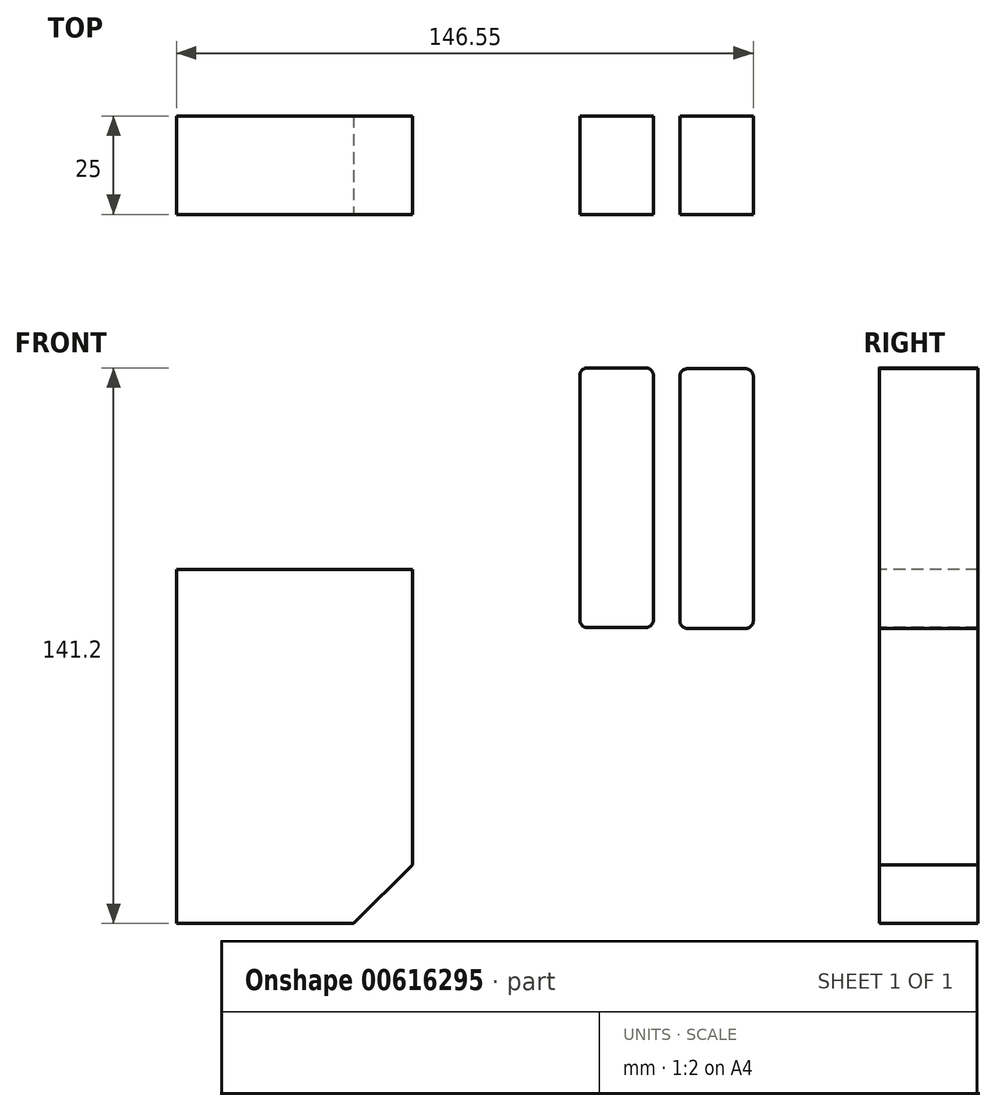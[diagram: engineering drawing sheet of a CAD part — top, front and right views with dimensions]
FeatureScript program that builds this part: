
annotation { "Feature Type Name" : "Feature", "Feature Type Description" : "" }
export const myFeature = defineFeature(function(context is Context, id is Id, definition is map)
    precondition{}
    {
        {
            var Q0;
            Q0=qCreatedBy(makeId("Front.planeOp"),FACE);
            var sketch = newSketch(context, id + "F0", { "sketchPlane" : qUnion([Q0])});
            skLineSegment(sketch, "E0.0", {"start": v(0, -90) * mm, "end": v(45, -90) * mm});
            skLineSegment(sketch, "E0.1", {"start": v(0, 0) * mm, "end": v(0, -90) * mm});
            skLineSegment(sketch, "E0.2", {"start": v(45, -90) * mm, "end": v(60, -75.15) * mm});
            skLineSegment(sketch, "E0.3", {"start": v(60, -75.15) * mm, "end": v(60, 0) * mm});
            skLineSegment(sketch, "E0.4", {"start": v(60, 0) * mm, "end": v(0, 0) * mm});
            skLineSegment(sketch, "E1.bottom", {"start": v(102.46, 51.2) * mm, "end": v(121.16, 51.2) * mm});
            skLineSegment(sketch, "E1.top", {"start": v(102.46, -14.8) * mm, "end": v(121.16, -14.8) * mm});
            skLineSegment(sketch, "E1.left", {"start": v(102.46, 51.2) * mm, "end": v(102.46, -14.8) * mm});
            skLineSegment(sketch, "E1.right", {"start": v(121.16, 51.2) * mm, "end": v(121.16, -14.8) * mm});
            skLineSegment(sketch, "E2.bottom", {"start": v(127.85, 50.99) * mm, "end": v(146.55, 50.99) * mm});
            skLineSegment(sketch, "E2.top", {"start": v(127.85, -15.01) * mm, "end": v(146.55, -15.01) * mm});
            skLineSegment(sketch, "E2.left", {"start": v(127.85, 50.99) * mm, "end": v(127.85, -15.01) * mm});
            skLineSegment(sketch, "E2.right", {"start": v(146.55, 50.99) * mm, "end": v(146.55, -15.01) * mm});
            skLineSegment(sketch, "E3.0", {"start": v(43.77, -87) * mm, "end": v(57, -73.9) * mm});
            skLineSegment(sketch, "E3.1", {"start": v(3, -87) * mm, "end": v(43.77, -87) * mm});
            skLineSegment(sketch, "E3.2", {"start": v(57, -73.9) * mm, "end": v(57, -3) * mm});
            skLineSegment(sketch, "E3.3", {"start": v(57, -3) * mm, "end": v(3, -3) * mm});
            skLineSegment(sketch, "E3.4", {"start": v(3, -3) * mm, "end": v(3, -87) * mm});
            skSolve(sketch);
        }
        {
            var Q0;
            Q0=sQuery(id+"F0.wireOp",EDGE,"E2.right");
            var Q1;
            Q1=sQuery(id+"F0.wireOp",EDGE,"E1.top");
            var Q2;
            Q2=sQuery(id+"F0.wireOp",EDGE,"E1.bottom");
            var Q3;
            Q3=sQuery(id+"F0.wireOp",EDGE,"E2.top");
            var Q4;
            Q4=sQuery(id+"F0.wireOp",EDGE,"E2.left");
            var Q5;
            Q5=sQuery(id+"F0.wireOp",EDGE,"E1.right");
            var Q6;
            Q6=sQuery(id+"F0.wireOp",EDGE,"E2.bottom");
            var Q7;
            Q7=sQuery(id+"F0.wireOp",EDGE,"E1.left");
            var Q8;
            Q8=sQuery(id+"F0.wireOp",EDGE,"E0.2");
            var Q9;
            Q9=sQuery(id+"F0.wireOp",EDGE,"E0.1");
            var Q10;
            Q10=sQuery(id+"F0.wireOp",EDGE,"E0.3");
            var Q11;
            Q11=sQuery(id+"F0.wireOp",EDGE,"E0.4");
            var Q12;
            Q12=sQuery(id+"F0.wireOp",EDGE,"E0.0");
            extrude(context, id + "F1", {"bodyType" : ToolBodyType.SURFACE, "surfaceEntities" : qUnion([Q0, Q1, Q2, Q3, Q4, Q5, Q6, Q7, Q8, Q9, Q10, Q11, Q12]), "depth" : 25 * mm, "offsetDistance" : 25 * mm});
        }
        {
            var Q0;
            Q0=makeQuery(id+"F1.opExtrude","SWEPT_EDGE",EDGE,{"disambiguationData":[OSD([sQuery(id+"F0.wireOp",VERTEX,"E2.bottom.start")])]});
            var Q1;
            Q1=makeQuery(id+"F1.opExtrude","SWEPT_FACE",FACE,{"disambiguationData":[OSD([sQuery(id+"F0.wireOp",EDGE,"E2.bottom")])]});
            var Q2;
            Q2=makeQuery(id+"F1.opExtrude","SWEPT_EDGE",EDGE,{"disambiguationData":[OSD([sQuery(id+"F0.wireOp",VERTEX,"E2.bottom.end")])]});
            var Q3;
            Q3=makeQuery(id+"F1.opExtrude","SWEPT_FACE",FACE,{"disambiguationData":[OSD([sQuery(id+"F0.wireOp",EDGE,"E2.top")])]});
            var Q4;
            Q4=makeQuery(id+"F1.opExtrude","SWEPT_FACE",FACE,{"disambiguationData":[OSD([sQuery(id+"F0.wireOp",EDGE,"E2.left")])]});
            var Q5;
            Q5=makeQuery(id+"F1.opExtrude","SWEPT_EDGE",EDGE,{"disambiguationData":[OSD([sQuery(id+"F0.wireOp",VERTEX,"E2.left.end")])]});
            var Q6;
            Q6=makeQuery(id+"F1.opExtrude","SWEPT_FACE",FACE,{"disambiguationData":[OSD([sQuery(id+"F0.wireOp",EDGE,"E2.right")])]});
            var Q7;
            Q7=makeQuery(id+"F1.opExtrude","SWEPT_EDGE",EDGE,{"disambiguationData":[OSD([sQuery(id+"F0.wireOp",VERTEX,"E1.right.end")])]});
            var Q8;
            Q8=makeQuery(id+"F1.opExtrude","SWEPT_EDGE",EDGE,{"disambiguationData":[OSD([sQuery(id+"F0.wireOp",VERTEX,"E1.right.start")])]});
            var Q9;
            Q9=makeQuery(id+"F1.opExtrude","SWEPT_FACE",FACE,{"disambiguationData":[OSD([sQuery(id+"F0.wireOp",EDGE,"E1.top")])]});
            var Q10;
            Q10=makeQuery(id+"F1.opExtrude","SWEPT_EDGE",EDGE,{"disambiguationData":[OSD([sQuery(id+"F0.wireOp",VERTEX,"E1.left.end")])]});
            var Q11;
            Q11=makeQuery(id+"F1.opExtrude","SWEPT_FACE",FACE,{"disambiguationData":[OSD([sQuery(id+"F0.wireOp",EDGE,"E1.bottom")])]});
            var Q12;
            Q12=makeQuery(id+"F1.opExtrude","SWEPT_EDGE",EDGE,{"disambiguationData":[OSD([sQuery(id+"F0.wireOp",VERTEX,"E1.left.start")])]});
            var Q13;
            Q13=makeQuery(id+"F1.opExtrude","SWEPT_FACE",FACE,{"disambiguationData":[OSD([sQuery(id+"F0.wireOp",EDGE,"E1.right")])]});
            var Q14;
            Q14=makeQuery(id+"F1.opExtrude","SWEPT_FACE",FACE,{"disambiguationData":[OSD([sQuery(id+"F0.wireOp",EDGE,"E1.left")])]});
            fillet(context, id + "F2", {"entities" : qUnion([Q0, Q1, Q2, Q3, Q4, Q5, Q6, Q7, Q8, Q9, Q10, Q11, Q12, Q13, Q14]), "radius" : 2 * mm, "tangentPropagation" : true, "allowEdgeOverflow" : false});
        }
    });
